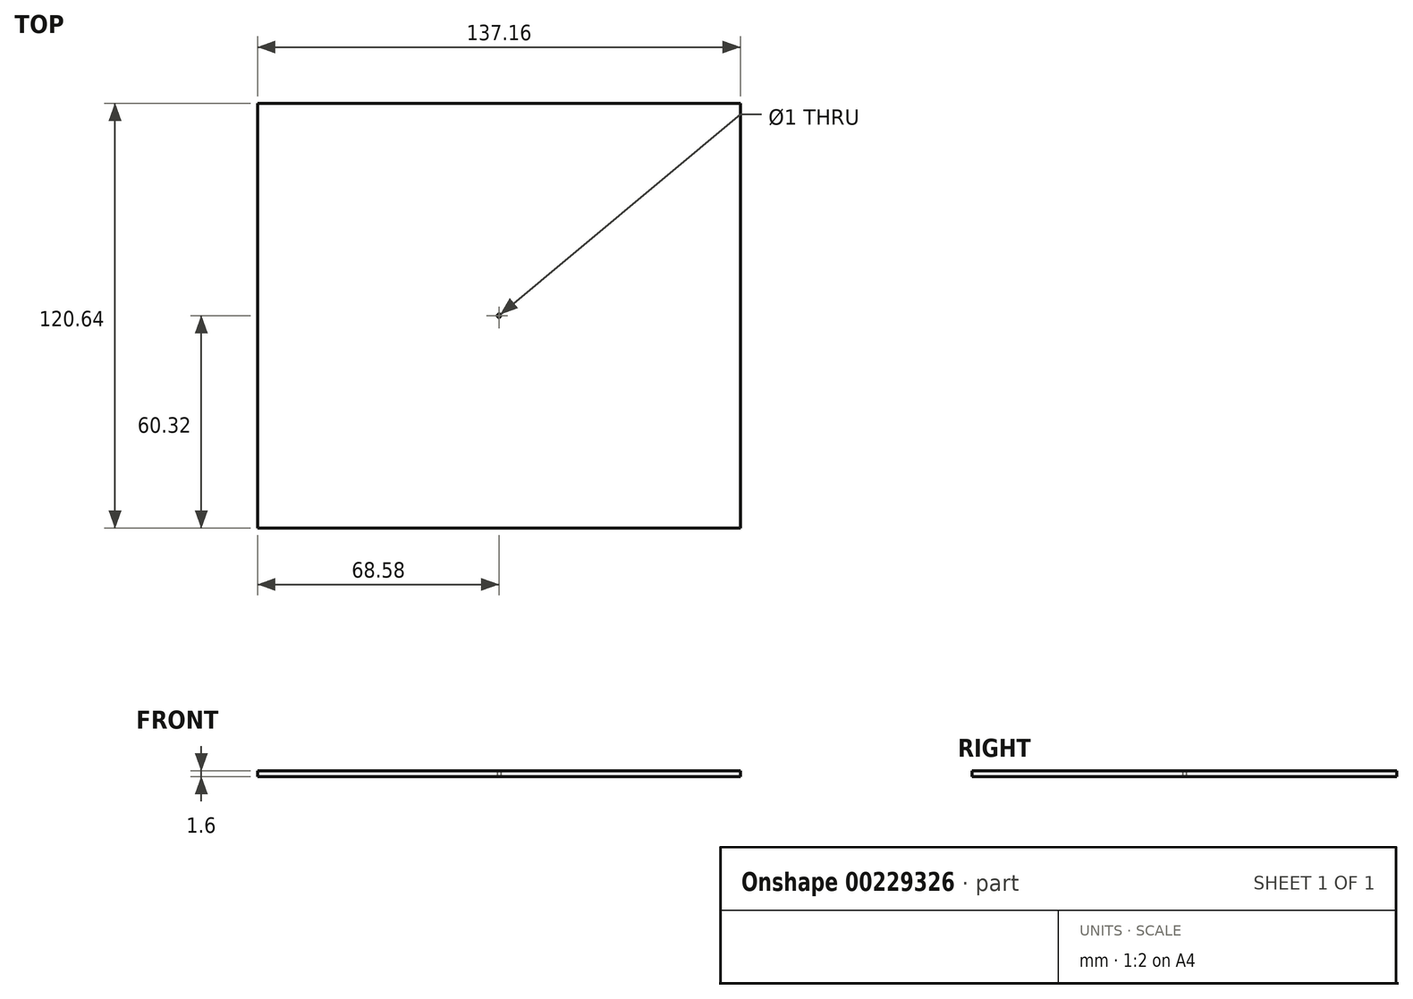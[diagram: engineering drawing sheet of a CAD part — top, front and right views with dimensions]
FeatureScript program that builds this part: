
annotation { "Feature Type Name" : "Feature", "Feature Type Description" : "" }
export const myFeature = defineFeature(function(context is Context, id is Id, definition is map)
    precondition{}
    {
        {
            var Q0;
            Q0=qCreatedBy(makeId("Top.planeOp"),FACE);
            var sketch = newSketch(context, id + "F0", { "sketchPlane" : qUnion([Q0])});
            skLineSegment(sketch, "E0.bottom", {"start": v(68.58, -60.32) * mm, "end": v(-68.58, -60.33) * mm});
            skLineSegment(sketch, "E0.top", {"start": v(68.58, 60.33) * mm, "end": v(-68.58, 60.33) * mm});
            skLineSegment(sketch, "E0.left", {"start": v(68.58, -60.32) * mm, "end": v(68.58, 60.33) * mm});
            skLineSegment(sketch, "E0.right", {"start": v(-68.58, -60.33) * mm, "end": v(-68.58, 60.33) * mm});
            skPoint(sketch, "E0.middle", {"position": v(0, 0) * mm});
            skCircle(sketch, "E1", {"center": v(0, 0) * mm, "radius": 0.5 * mm});
            skSolve(sketch);
        }
        {
            var Q0;
            Q0 = qSketchRegion(id + "F0", true);
            extrude(context, id + "F1", {"entities" : qUnion([Q0]), "depth" : 1.6 * mm});
        }
    });
